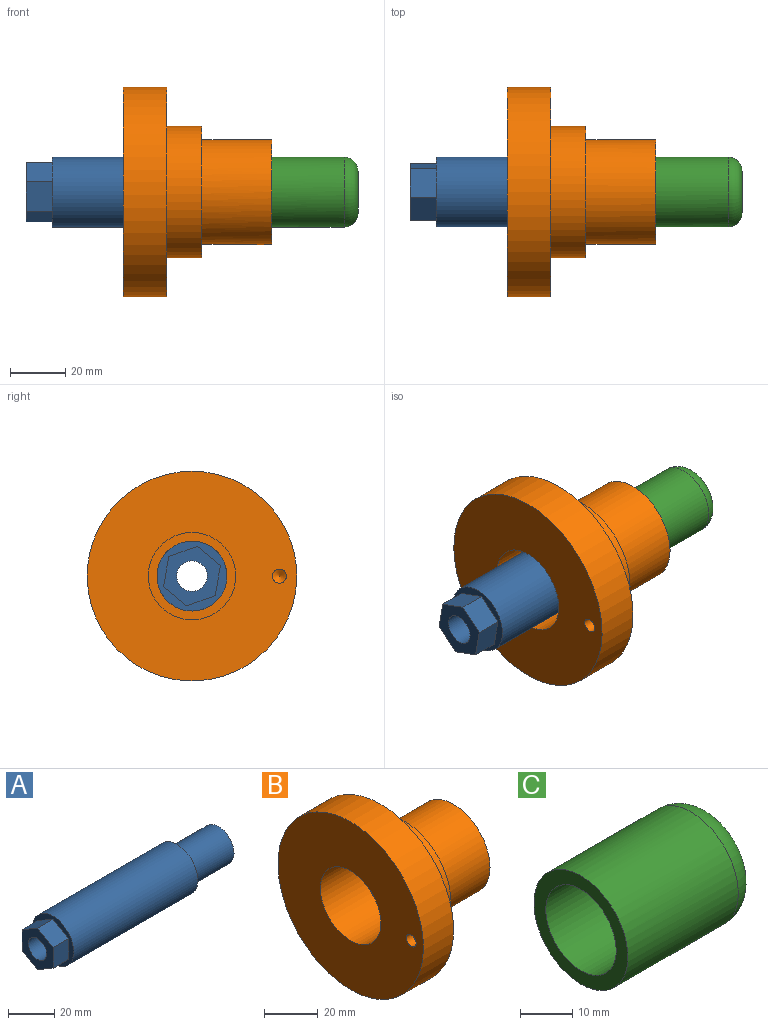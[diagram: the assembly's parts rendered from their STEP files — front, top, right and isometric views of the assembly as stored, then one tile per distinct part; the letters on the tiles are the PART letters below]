
ASSEMBLY  parts=3 mates=2
PART A: 13 faces, bbox 111.1x25.4x25.4 mm
  f0: plane 19.05x19.05mm, normal (1,0,0), area 188mm2, adj f1,f12
  f1: cylinder r=9.53mm len=25.4mm, axis (-1,0,0), area 1520.1mm2, adj f0,f2
  f2: plane 25.4x25.4mm, normal (1,0,0), area 221.7mm2, adj f1,f3
  f3: cylinder r=12.7mm len=76.2mm, axis (-1,0,0), area 6080.5mm2, adj f2,f4
  f4: plane 25.4x25.4mm, normal (-1,0,0), area 192.4mm2, adj f3,f5,f6,f7,f8,f9,f10
  f5: plane 9.53x9.53mm, normal (0,-0.5,-0.87), area 104.8mm2, adj f4,f6,f10,f11
  f6: plane 11x9.53mm, normal (0,-1,0), area 104.8mm2, adj f4,f5,f7,f11
  f7: plane 9.53x9.53mm, normal (0,-0.5,0.87), area 104.8mm2, adj f4,f6,f8,f11
  f8: plane 9.53x9.53mm, normal (0,0.5,0.87), area 104.8mm2, adj f4,f7,f9,f11
  f9: plane 11x9.53mm, normal (0,1,0), area 104.8mm2, adj f4,f8,f10,f11
  f10: plane 9.53x9.53mm, normal (0,0.5,-0.87), area 104.8mm2, adj f4,f5,f9,f11
  f11: plane 22x19.05mm, normal (-1,0,0), area 217.3mm2, adj f5,f6,f7,f8,f9,f10,f12
  f12: cylinder r=5.56mm len=111.13mm, axis (-1,0,0), area 3879.5mm2, adj f0,f11
PART B: 12 faces, bbox 54x76.2x76.2 mm
  f0: cylinder r=19.05mm len=38.1mm, axis (-1,0,0), area 3040.2mm2, adj f2,f6
  f1: cylinder r=12.7mm len=31.75mm, axis (-1,0,0), area 2533.5mm2, adj f2,f4
  f2: plane 38.1x38.1mm, normal (1,0,0), area 633.4mm2, adj f0,f1
  f3: cylinder r=15.88mm len=31.75mm, axis (-1,0,0), area 2216.8mm2, adj f4,f8
  f4: plane 31.75x31.75mm, normal (-1,0,0), area 285mm2, adj f1,f3
  f5: cylinder r=23.88mm len=47.75mm, axis (-1,0,0), area 1905.2mm2, adj f6,f9
  f6: plane 47.75x47.75mm, normal (1,0,0), area 650.8mm2, adj f0,f5
  f7: cylinder r=38.1mm len=76.2mm, axis (1,0,0), area 3800.3mm2, adj f8,f9
  f8: plane 76.2x76.2mm, normal (-1,0,0), area 3748.2mm2, adj f3,f7,f11
  f9: plane 76.2x76.2mm, normal (1,0,0), area 2769.5mm2, adj f5,f7
  f10: cone r=0mm half-angle=59deg, axis (-1,0,0), area 23.9mm2, adj f11
  f11: cylinder r=2.55mm len=12.7mm, axis (-1,0,0), area 203.7mm2, adj f8,f10
PART C: 7 faces, bbox 34.9x27.5x27.5 mm
  f0: cylinder r=12.7mm len=29.85mm, axis (1,0,0), area 2381.5mm2, adj f1,f5
  f1: plane 25.4x25.4mm, normal (-1,0,0), area 221.7mm2, adj f0,f2
  f2: cylinder r=9.53mm len=25.4mm, axis (1,0,0), area 1520.1mm2, adj f1,f3
  f3: plane 19.05x19.05mm, normal (-1,0,0), area 188mm2, adj f2,f6
  f4: plane 15.24x15.24mm, normal (1,0,0), area 85.4mm2, adj f5,f6
  f5: torus R=7.62mm, axis (-1,0,0), area 544.2mm2, adj f0,f4
  f6: cylinder r=5.56mm len=11.11mm, axis (-1,0,0), area 332.5mm2, adj f3,f4
PLACE A rot(axis=(1,0,0),129.9deg) t=(-69.75,-0.27,-14.6)mm
PLACE B t=(-40.77,-0.27,-14.6)mm fixed
PLACE C rot(axis=(1,0,0),129.9deg) t=(-69.75,-0.27,-14.6)mm
MATE cylindrical B.f1 <-> A.f1  axis (-1,0,0) through (-34.42,-0.27,-14.6)mm
MATE fastened A.f1 <-> C.f0  axis (1,0,0) through (19.15,-0.27,-14.6)mm
